# Revit family: 706140001_Espejo Retractil
name_source: partatom
category: Plumbing Fixtures
units: mm (PartAtom-declared; Revit-internal decimal feet)

## family parameters
Always vertical = Yes
Cut with Voids When Loaded = No
Host = Wall
OmniClass Number = 23.21.37.13.15
OmniClass Title = Mirrors
Part Type = Normal
Room Calculation Point = No
Round Connector Dimension = Use Diameter
Shared = No

## types (1)
- Type 1
    Alto = 376 mm  [stored 1.2336 ft]
    Ancho = 350 mm  [stored 1.14829 ft]
    Aumento Espejo = 2,5 veces y giratorio 360°.
    Creado por = BIMBAU
    Cuerpo = Giratorio 360°.
    Cuidados y Limpieza Espejo = 1. Utilizar 1 parte de vinagre por 5 de agua. 2. Evitar los rayones. 3. Realizar limpieza al espejo al menos tres (3)días por semana.
    Default Elevation = 0 mm  [stored 0 ft]
    Description = Con capacidad de aumento de hasta 2.5 veces y cuerpo giratorio 360° este espejo es el ideal para tu hotel.
    Diametro Espejo = 186 mm.
    Fecha de creación = 13/04/2021
    Funcionalidad = Cuerpo Giratorio y adaptable a cualquier espacio
    Garantía = 2 Años
    Manufacturer = Corona
    Material = Corona_Espejo
    Material 2 = Corona_Aluminio
    Model = Espejo de una pieza
    Normatividad = NTC 5339.
    Referencia = 706140001
    Resistencia a cargas = 55 Lbf.
    Tipo de instalación = A muro
    URL = https://corona.co
    Uso = Libre de bordes filosos u otras irregularidades.

note: [stored X ft] marks values corroborated as IEEE doubles in the binary element streams (Revit-internal decimal feet)

## geometry (parser evidence)
native form markers: Sweep x5
no freeform markers — native parametric forms only
